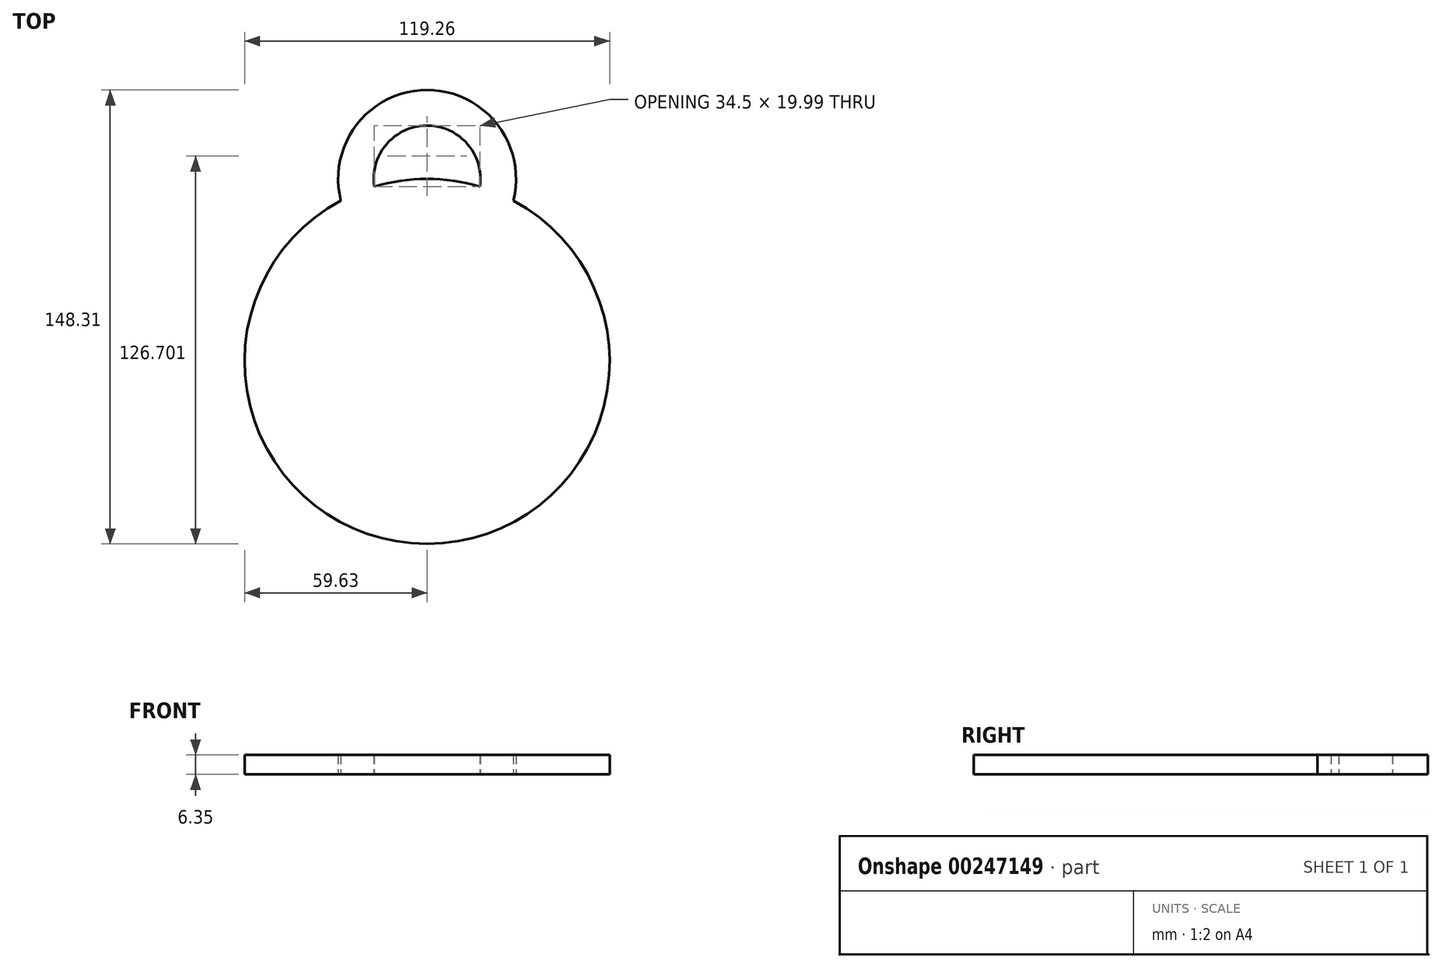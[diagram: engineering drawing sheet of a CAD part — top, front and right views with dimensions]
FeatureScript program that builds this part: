
annotation { "Feature Type Name" : "Feature", "Feature Type Description" : "" }
export const myFeature = defineFeature(function(context is Context, id is Id, definition is map)
    precondition{}
    {
        {
            var Q0;
            Q0=qCreatedBy(makeId("Top.planeOp"),FACE);
            var sketch = newSketch(context, id + "F0", { "sketchPlane" : qUnion([Q0])});
            skArc(sketch, "E0", {"start": v(17.25, 57.08) * mm, "mid": v(0, 59.63) * mm, "end": v(-17.25, 57.08) * mm});
            skArc(sketch, "E1", {"start": v(28.17, 52.55) * mm, "mid": v(0, 88.68) * mm, "end": v(-28.17, 52.55) * mm});
            skArc(sketch, "E2", {"start": v(17.25, 57.08) * mm, "mid": v(0, 77.07) * mm, "end": v(-17.25, 57.08) * mm});
            skArc(sketch, "E3.trimOffspring", {"start": v(-28.17, 52.55) * mm, "mid": v(0, -59.63) * mm, "end": v(28.17, 52.55) * mm});
            skSolve(sketch);
        }
        {
            var Q0;
            Q0=makeQuery(id+"F0.imprint","IMPRINT",FACE,{"disambiguationData":[TD([[makeQuery(id+"F0.imprint","IMPRINT",EDGE,{"derivedFrom":sQuery(id+"F0.wireOp",EDGE,"E0")}),1.0]])]});
            extrude(context, id + "F1", {"entities" : qUnion([Q0]), "depth" : 6.35 * mm});
        }
        {
            var Q0;
            Q0=qCreatedBy(makeId("Top.planeOp"),FACE);
            var sketch = newSketch(context, id + "F2", { "sketchPlane" : qUnion([Q0])});
            skCircle(sketch, "E4", {"center": v(0, 0) * mm, "radius": 52.62 * mm});
            skSolve(sketch);
        }
        {
            var Q0;
            Q0=sQuery(id+"F2.wireOp",EDGE,"E4");
            extrude(context, id + "F3", {"bodyType" : ToolBodyType.SURFACE, "surfaceEntities" : qUnion([Q0]), "depth" : 12.7 * mm});
        }
        {
            var Q0;
            Q0=qCreatedBy(makeId("Top.planeOp"),FACE);
            var sketch = newSketch(context, id + "F4", { "sketchPlane" : qUnion([Q0])});
            skCircle(sketch, "E5", {"center": v(0, 0) * mm, "radius": 45.95 * mm});
            skCircle(sketch, "E6", {"center": v(0, 0) * mm, "radius": 39.78 * mm});
            skCircle(sketch, "E7", {"center": v(0, 0) * mm, "radius": 50.61 * mm});
            skCircle(sketch, "E8", {"center": v(0, 0) * mm, "radius": 48.32 * mm});
            skCircle(sketch, "E9", {"center": v(0, 0) * mm, "radius": 44.33 * mm});
            skCircle(sketch, "E10", {"center": v(0, 0) * mm, "radius": 42.1 * mm});
            skSolve(sketch);
        }
        {
            var Q0;
            Q0=sQuery(id+"F4.wireOp",EDGE,"E7");
            var Q1;
            Q1=sQuery(id+"F4.wireOp",EDGE,"E8");
            var Q2;
            Q2=sQuery(id+"F4.wireOp",EDGE,"E5");
            var Q3;
            Q3=sQuery(id+"F4.wireOp",EDGE,"E9");
            var Q4;
            Q4=sQuery(id+"F4.wireOp",EDGE,"E10");
            var Q5;
            Q5=sQuery(id+"F4.wireOp",EDGE,"E6");
            extrude(context, id + "F5", {"bodyType" : ToolBodyType.SURFACE, "surfaceEntities" : qUnion([Q0, Q1, Q2, Q3, Q4, Q5]), "depth" : 10.16 * mm});
        }
    });
